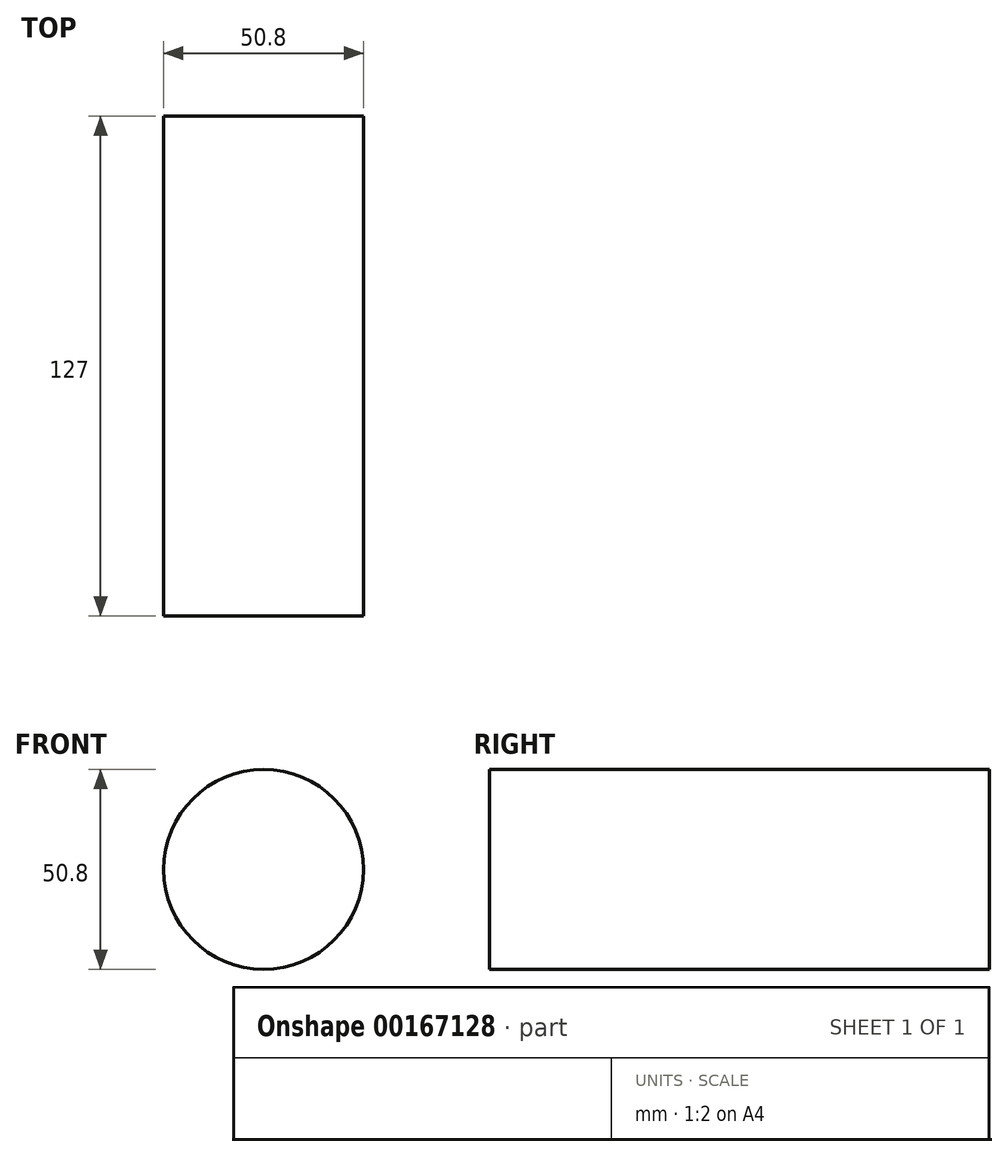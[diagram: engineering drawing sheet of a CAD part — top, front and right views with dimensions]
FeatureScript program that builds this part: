
annotation { "Feature Type Name" : "Feature", "Feature Type Description" : "" }
export const myFeature = defineFeature(function(context is Context, id is Id, definition is map)
    precondition{}
    {
        {
            var Q0;
            Q0=qCreatedBy(makeId("Front.planeOp"),FACE);
            var sketch = newSketch(context, id + "F0", { "sketchPlane" : qUnion([Q0])});
            skCircle(sketch, "E0", {"center": v(0, 0) * mm, "radius": 25.4 * mm});
            skSolve(sketch);
        }
        {
            var Q0;
            Q0 = qSketchRegion(id + "F0", true);
            var Q1;
            Q1=makeQuery(id+"F0.imprint","IMPRINT",FACE,{"disambiguationData":[TD([[makeQuery(id+"F0.imprint","IMPRINT",EDGE,{"derivedFrom":sQuery(id+"F0.wireOp",EDGE,"E0")}),1.0]])]});
            extrude(context, id + "F1", {"entities" : qUnion([Q0, Q1]), "endBound" : BoundingType.SYMMETRIC, "depth" : 127 * mm});
        }
    });
